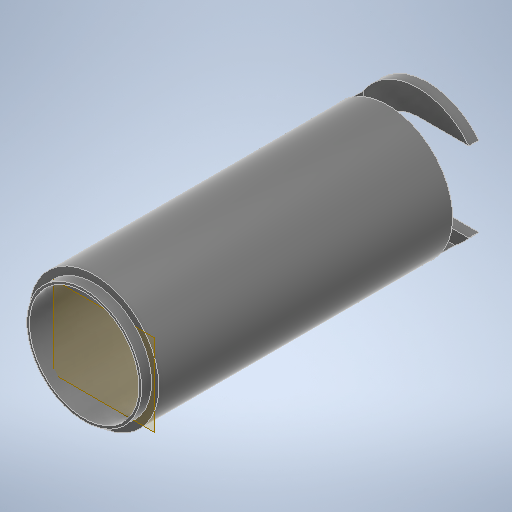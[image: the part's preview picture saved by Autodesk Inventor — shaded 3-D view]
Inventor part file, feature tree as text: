
AUTODESK INVENTOR PART (.ipt)
format: ipt  version: 2025.1 (Build 291241020, 241B)  size: 662,528 bytes
history: native  units: mm
features: extrude x9, sketch x9, plane x1, mirror x1
ambient origin geometry x8: Origin, YZ Plane, XZ Plane, XY Plane, X Axis, Y Axis, Z Axis, Center Point
bodies: Solid1 (feature_tree)
feature tree (20):
  extrude  "Extrusion1"  Depth=39.0mm
  plane  "Work Plane1"
  extrude  "Extrusion2"  Depth=3.0mm TaperAngle=0.0deg
  mirror  "Mirror1"
  extrude  "Extrusion5"  Depth=10.0mm TaperAngle=0.0deg
  extrude  "Extrusion6"  Depth=9.0mm
  extrude  "Extrusion7"  Depth=20.0mm
  extrude  "Extrusion8"  TaperAngle=0.0deg  [1 undecoded]
  extrude  "Extrusion9"  Depth=33.0mm
  extrude  "Extrusion10"  TaperAngle=0.0deg  [1 undecoded]
  extrude  "Extrusion12"  [1 undecoded]
  sketch  "Sketch1"  dims[d0=33.0mm d1=39.0mm]
  sketch  "Sketch2"  dims[d2=195.0mm d3=0.0mm d4=3.0mm d5=0.0mm]
  sketch  "Sketch5"  dims[d12=24.0mm d13=10.0mm d14=0.0mm]
  sketch  "Sketch6"  dims[d15=0.0mm d16=0.0mm d17=9.0mm]
  sketch  "Sketch7"  dims[d18=0.0mm d19=0.0mm d20=20.0mm]
  sketch  "Sketch8"  dims[d21=5.0mm d22=0.0mm d23=0.0mm d24=0.0mm]
  sketch  "Sketch9"  dims[d25=0.8mm d26=33.0mm]
  sketch  "Sketch10"  dims[d28=3.0mm d29=0.0mm d33=0.0mm d34=0.0mm]
  sketch  "Sketch12"
note: 3 required parameter values undecoded (feature->parameter linkage not recoverable at this tier; creation-order binding heuristic only, values carry confidence <= 0.55)
